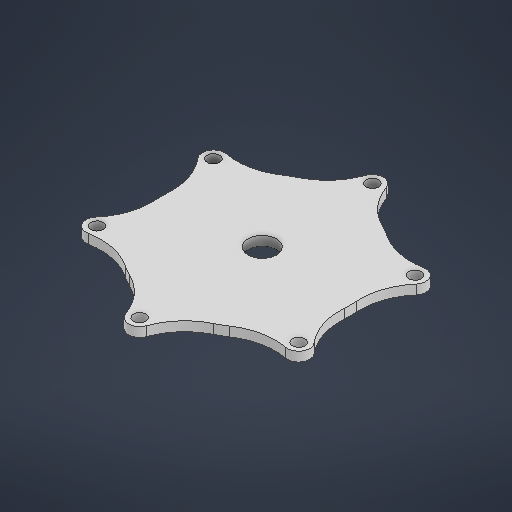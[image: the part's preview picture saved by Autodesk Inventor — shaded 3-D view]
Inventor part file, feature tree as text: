
AUTODESK INVENTOR PART (.ipt)
format: ipt  version: 2025.3 (Build 293356000, 356)  size: 260,096 bytes
history: native  units: mm
features: sketch x3, extrude x3
ambient origin geometry x8: Origin, YZ Plane, XZ Plane, XY Plane, X Axis, Y Axis, Z Axis, Center Point
bodies: Body1 (feature_tree)
feature tree (6):
  sketch  "Sketch1"  dims[d16=60.0mm d17=55.0mm]
  extrude  "Extrusion5"  Depth=55.0mm
  extrude  "Extrusion6"  Depth=37.0mm
  extrude  "Extrusion12"  Depth=2.0mm
  sketch  "Sketch Circular Pattern1"  dims[d18=7.0mm d19=37.0mm]
  sketch  "Sketch10"  dims[d21=20.0mm d22=4.0mm d23=60.0mm d25=360.0deg d27=3.0mm d28=0.0mm d29=3.0mm d30=0.0mm d58=9.0mm d59=45.0mm d60=2.0mm d61=20.25mm d62=0.0mm d3=0.5mm d4=0.872665mm d5=0.5mm d6=0.872665mm d39=0.5mm d40=0.872665mm d41=0.5mm d42=0.872665mm]
